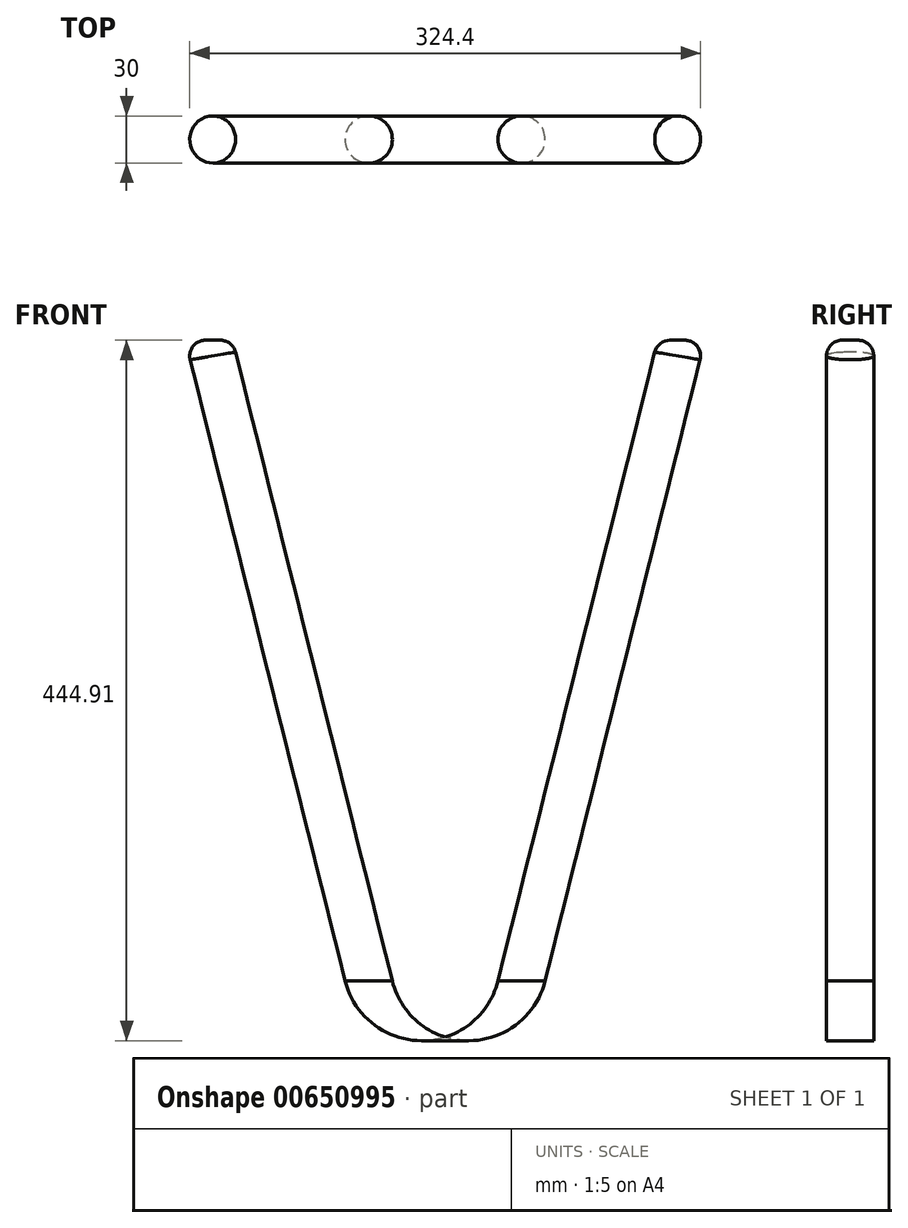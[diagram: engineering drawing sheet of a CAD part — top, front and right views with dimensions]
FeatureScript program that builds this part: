
annotation { "Feature Type Name" : "Feature", "Feature Type Description" : "" }
export const myFeature = defineFeature(function(context is Context, id is Id, definition is map)
    precondition{}
    {
        {
            var Q0;
            Q0=qCreatedBy(makeId("Front.planeOp"),FACE);
            var sketch = newSketch(context, id + "F0", { "sketchPlane" : qUnion([Q0])});
            skLineSegment(sketch, "E0", {"start": v(340.22, -199.87) * mm, "end": v(441.7, 207.14) * mm});
            skLineSegment(sketch, "E1", {"start": v(141.7, 207.14) * mm, "end": v(243.2, -199.87) * mm});
            skPoint(sketch, "E2.visualSharp", {"position": v(291.7, -394.44) * mm});
            skArc(sketch, "E2.filletArc", {"start": v(243.2, -199.87) * mm, "mid": v(291.7, -237.77) * mm, "end": v(340.22, -199.87) * mm});
            skLineSegment(sketch, "E3", {"start": v(291.7, -237.77) * mm, "end": v(291.7, 694.44) * mm});
            skPoint(sketch, "E3.startSnap0", {"position": v(291.7, -237.77) * mm});
            skSolve(sketch);
        }
        {
            var Q0;
            Q0=qCreatedBy(makeId("Top.planeOp"),FACE);
            var sketch = newSketch(context, id + "F1", { "sketchPlane" : qUnion([Q0])});
            skCircle(sketch, "E4", {"center": v(-120.3, 0) * mm, "radius": 15 * mm});
            skSolve(sketch);
        }
        {
            var Q0;
            Q0=makeQuery(id+"F1.imprint","IMPRINT",FACE,{"disambiguationData":[TD([[makeQuery(id+"F1.imprint","IMPRINT",EDGE,{"derivedFrom":sQuery(id+"F1.wireOp",EDGE,"E4")}),1.0]])]});
            var Q1;
            Q1=sQuery(id+"F0.wireOp",EDGE,"E1");
            var Q2;
            Q2=sQuery(id+"F0.wireOp",EDGE,"E2.filletArc");
            var Q3;
            Q3=sQuery(id+"F0.wireOp",EDGE,"E0");
            sweep(context, id + "F2", {"profiles" : qUnion([Q0]), "path" : qUnion([Q1, Q2, Q3]), "keepProfileOrientation" : true});
        }
        {
            var Q0;
            Q0=makeQuery(id+"F2.opSweep","CAP_EDGE",EDGE,{"disambiguationData":[OSD([sQuery(id+"F0.wireOp",VERTEX,"E1.start"),sQuery(id+"F1.wireOp",EDGE,"E4")])],"isStart":false});
            var Q1;
            Q1=makeQuery(id+"F2.opSweep","CAP_EDGE",EDGE,{"disambiguationData":[OSD([sQuery(id+"F0.wireOp",VERTEX,"E0.end"),sQuery(id+"F1.wireOp",EDGE,"E4")])],"isStart":true});
            fillet(context, id + "F3", {"entities" : qUnion([Q0, Q1]), "radius" : 10 * mm, "tangentPropagation" : true, "allowEdgeOverflow" : false});
        }
    });
